# Revit family: Urinal-Wall_Mount-KOHLER-DEXTER-K-5016T_1
name_source: partatom
category: Plumbing Fixtures
revit_build: Autodesk Revit 2017 (Build: 20160225_1515(x64)
units: mm (PartAtom-declared; Revit-internal decimal feet)

## family parameters
Cut with Voids When Loaded = No
Host = Face
OmniClass Number = 23.31.21.00
OmniClass Title = Urinals
Part Type = Normal
Room Calculation Point = No
Round Connector Dimension = Use Diameter
Shared = No

## types (9) — shared parameters
Assembly Code = D2010200
CW Connection = Yes
Cold Water Inlet = Cold Water Inlet
Date Modified = 07/06/2020
Default Elevation = 0"
Flow Rate = 0 GPM
HW Connection = No
Height = 20 3/8"
Hot Water Inlet = Hot Water Inlet
Length = 14 1/2"
Manufacturer = KOHLER Co.
Master Format 2014 = 22 41 13.16
Master Format 2014 Name = Residential Urinals
Material = Vitreous China
Pressure = 0.00 psi
Product Name = DEXTER
URL = http://www.kohler.com.cn
Vent Connection = No
Waste Connection = Yes
Waste Water Outlet = Waste Water Outlet
WaterSense Certified = No
Width = 13 5/8"

## per-type parameters (varying)
| type | Cut Depth | Description | ER | ET | Finish | Flush Rate- GPF | Flush Rate- LPF | Model | Product Documentation Link | Product Page URL | Type | YER | YET |
| ER-Rear Spud, 0-White | 3/4" | Rear Inlet Urinal | Yes | No | Kohler-Vitreous_China-0-White | 0.26 GPF | 1 LPF | K-5016T-ER-0 |  |  | 1 | No | No |
| ER-Rear Spud, 47-Almond | 3/4" | Rear Inlet Urinal | Yes | No | Kohler-Vitreous_China-47-Almond | 0.26 GPF | 1 LPF | K-5016T-ER-47 |  |  | 3 | No | No |
| ER-Rear Spud, 96-Biscuit | 3/4" | Rear Inlet Urinal | Yes | No | Kohler-Vitreous_China-96-Biscuit | 0.26 GPF | 1 LPF | K-5016T-ER-96 |  |  | 2 | No | No |
| ER-Rear Spud, 71-Seafoam | 3/4" | Rear Inlet Urinal | Yes | No | KOHLER-Vitreous_China-71-Seafoam | 0.26 GPF | 1 LPF | K-5016T-ER-71 |  |  | 4 | No | No |
| ET-Top Spud, 0-White | 0" | Top Inlet Urinal | No | Yes | Kohler-Vitreous_China-0-White | 0.26 GPF | 1 LPF | K-5016T-ET-0 |  |  | 5 | No | No |
| ET-Top Spud, 96-Biscuit | 0" | Top Inlet Urinal | No | Yes | Kohler-Vitreous_China-96-Biscuit | 0.26 GPF | 1 LPF | K-5016T-ET-96 |  |  | 6 | No | No |
| ET-Top Spud, 47-Almond | 0" | Top Inlet Urinal | No | Yes | Kohler-Vitreous_China-47-Almond | 0.26 GPF | 1 LPF | K-5016T-ET-47 |  |  | 7 | No | No |
| YER-Rear Spud, 0-White | 3/4" | Dust Super Water Saving Urinal | No | No | Kohler-Vitreous_China-0-White | 0.125 GPF | 0.5 LPF | K-5016T-YER-0 | https://files.kohler.com.cn | https://www.kohler.com.cn | 8 | Yes | No |
| YET-Top Spud, 0-White | 0" | Dust Super Water Saving Urinal | No | No | Kohler-Vitreous_China-0-White | 0.125 GPF | 0.5 LPF | K-5016T-YET-0 | https://files.kohler.com.cn | https://www.kohler.com.cn | 9 | No | Yes |

## geometry (parser evidence)
native form markers: Sweep x4
no freeform markers — native parametric forms only
